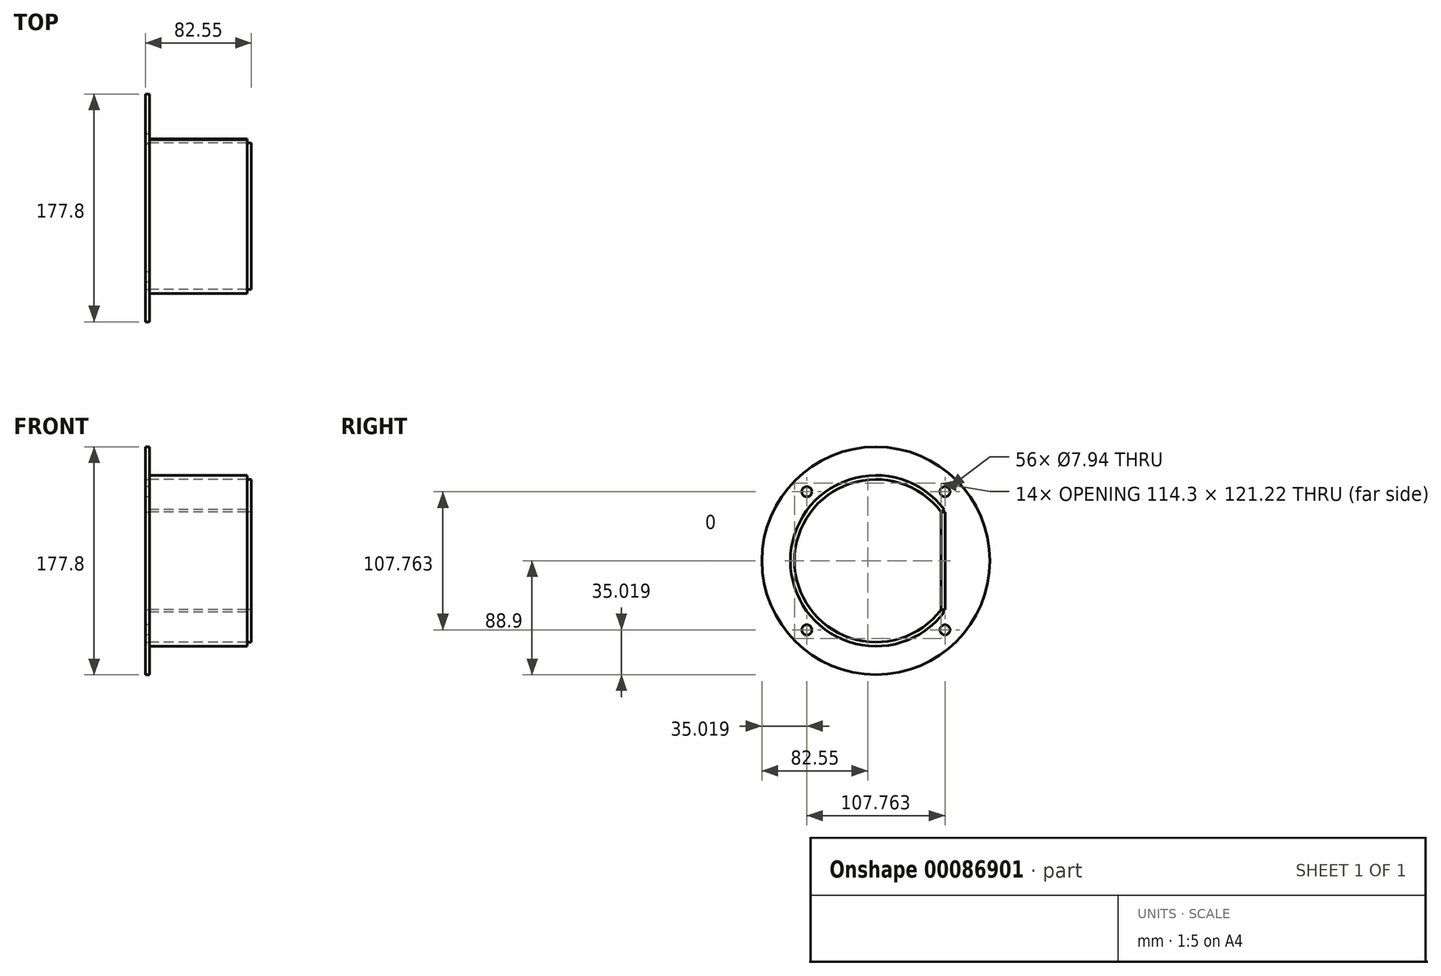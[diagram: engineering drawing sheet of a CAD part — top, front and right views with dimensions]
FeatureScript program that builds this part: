
annotation { "Feature Type Name" : "Feature", "Feature Type Description" : "" }
export const myFeature = defineFeature(function(context is Context, id is Id, definition is map)
    precondition{}
    {
        {
            var Q0;
            Q0=qCreatedBy(makeId("Right.planeOp"),FACE);
            var sketch = newSketch(context, id + "F0", { "sketchPlane" : qUnion([Q0])});
            skCircle(sketch, "E0", {"center": v(0, 0) * mm, "radius": 88.9 * mm});
            skCircle(sketch, "E1", {"center": v(0, 0) * mm, "radius": 76.2 * mm, "construction": true});
            skLineSegment(sketch, "E2", {"start": v(0, 0) * mm, "end": v(0, 105.34) * mm, "construction": true});
            skLineSegment(sketch, "E3", {"start": v(0, 0) * mm, "end": v(-90.27, 90.27) * mm, "construction": true});
            skCircle(sketch, "E4", {"center": v(-53.88, 53.88) * mm, "radius": 3.97 * mm});
            skCircle(sketch, "E5.1.0", {"center": v(-53.88, -53.88) * mm, "radius": 3.97 * mm});
            skCircle(sketch, "E5.2.0", {"center": v(53.88, -53.88) * mm, "radius": 3.97 * mm});
            skCircle(sketch, "E5.3.0", {"center": v(53.88, 53.88) * mm, "radius": 3.97 * mm});
            skSolve(sketch);
        }
        {
            var Q0;
            Q0 = qSketchRegion(id + "F0", true);
            extrude(context, id + "F1", {"entities" : qUnion([Q0]), "depth" : 3.17 * mm});
        }
        {
            var Q0;
            Q0=makeQuery(id+"F1.opExtrude","CAP_FACE",FACE,{"disambiguationData":[OSD([sQuery(id+"F0.wireOp",EDGE,"E0"),sQuery(id+"F0.wireOp",EDGE,"E4"),sQuery(id+"F0.wireOp",EDGE,"E5.1.0"),sQuery(id+"F0.wireOp",EDGE,"E5.2.0"),sQuery(id+"F0.wireOp",EDGE,"E5.3.0")])],"isStart":false});
            var sketch = newSketch(context, id + "F2", { "sketchPlane" : qUnion([Q0])});
            skArc(sketch, "E6", {"start": v(50.8, 38.1) * mm, "mid": v(-63.5, 0) * mm, "end": v(50.8, -38.1) * mm});
            skLineSegment(sketch, "E7", {"start": v(50.8, 38.1) * mm, "end": v(50.8, -38.1) * mm});
            skSolve(sketch);
        }
        {
            var Q0;
            Q0 = qSketchRegion(id + "F2", true);
            extrude(context, id + "F3", {"entities" : qUnion([Q0]), "operationType" : NewBodyOperationType.REMOVE, "endBound" : BoundingType.THROUGH_ALL, "oppositeDirection" : true, "depth" : 25.4 * mm});
        }
        {
            var Q0;
            Q0=makeQuery(id+"F1.opExtrude","CAP_FACE",FACE,{"disambiguationData":[OSD([sQuery(id+"F0.wireOp",EDGE,"E0"),sQuery(id+"F0.wireOp",EDGE,"E4"),sQuery(id+"F0.wireOp",EDGE,"E5.1.0"),sQuery(id+"F0.wireOp",EDGE,"E5.2.0"),sQuery(id+"F0.wireOp",EDGE,"E5.3.0")])],"isStart":false});
            var sketch = newSketch(context, id + "F4", { "sketchPlane" : qUnion([Q0])});
            skArc(sketch, "E8.0", {"start": v(50.8, 38.1) * mm, "mid": v(-63.5, 0) * mm, "end": v(50.8, -38.1) * mm});
            skArc(sketch, "E9.0", {"start": v(53.34, 40) * mm, "mid": v(-66.67, 0) * mm, "end": v(53.34, -40) * mm});
            skLineSegment(sketch, "E10", {"start": v(53.34, 40) * mm, "end": v(50.8, 38.1) * mm});
            skLineSegment(sketch, "E11", {"start": v(53.34, -40) * mm, "end": v(50.8, -38.1) * mm});
            skSolve(sketch);
        }
        {
            var Q0;
            Q0 = qSketchRegion(id + "F4", true);
            extrude(context, id + "F5", {"entities" : qUnion([Q0]), "depth" : 76.2 * mm});
        }
        {
            var Q0;
            Q0=makeQuery(id+"F1.opExtrude","CAP_FACE",FACE,{"disambiguationData":[OSD([sQuery(id+"F0.wireOp",EDGE,"E0"),sQuery(id+"F0.wireOp",EDGE,"E4"),sQuery(id+"F0.wireOp",EDGE,"E5.1.0"),sQuery(id+"F0.wireOp",EDGE,"E5.2.0"),sQuery(id+"F0.wireOp",EDGE,"E5.3.0")])],"isStart":false});
            var sketch = newSketch(context, id + "F6", { "sketchPlane" : qUnion([Q0])});
            skLineSegment(sketch, "E12.bottom", {"start": v(50.8, 38.1) * mm, "end": v(53.97, 38.1) * mm});
            skLineSegment(sketch, "E12.top", {"start": v(50.8, -38.1) * mm, "end": v(53.97, -38.1) * mm});
            skLineSegment(sketch, "E12.left", {"start": v(50.8, 38.1) * mm, "end": v(50.8, -38.1) * mm});
            skLineSegment(sketch, "E12.right", {"start": v(53.97, 38.1) * mm, "end": v(53.97, -38.1) * mm});
            skSolve(sketch);
        }
        {
            var Q0;
            Q0 = qSketchRegion(id + "F6", true);
            extrude(context, id + "F7", {"entities" : qUnion([Q0]), "depth" : 76.2 * mm});
        }
        {
            var Q0;
            Q0=makeQuery(id+"F5.opExtrude","CAP_FACE",FACE,{"disambiguationData":[OSD([sQuery(id+"F4.wireOp",EDGE,"E8.0"),sQuery(id+"F4.wireOp",EDGE,"E9.0"),sQuery(id+"F4.wireOp",EDGE,"E10"),sQuery(id+"F4.wireOp",EDGE,"E11")])],"isStart":false});
            var sketch = newSketch(context, id + "F8", { "sketchPlane" : qUnion([Q0])});
            skArc(sketch, "E13.0", {"start": v(50.8, 38.1) * mm, "mid": v(-63.5, 0) * mm, "end": v(50.8, -38.1) * mm});
            skLineSegment(sketch, "E14.0", {"start": v(50.8, 38.1) * mm, "end": v(50.8, -38.1) * mm});
            skSolve(sketch);
        }
        {
            var Q0;
            Q0 = qSketchRegion(id + "F8", true);
            extrude(context, id + "F9", {"entities" : qUnion([Q0]), "depth" : 3.17 * mm});
        }
    });
